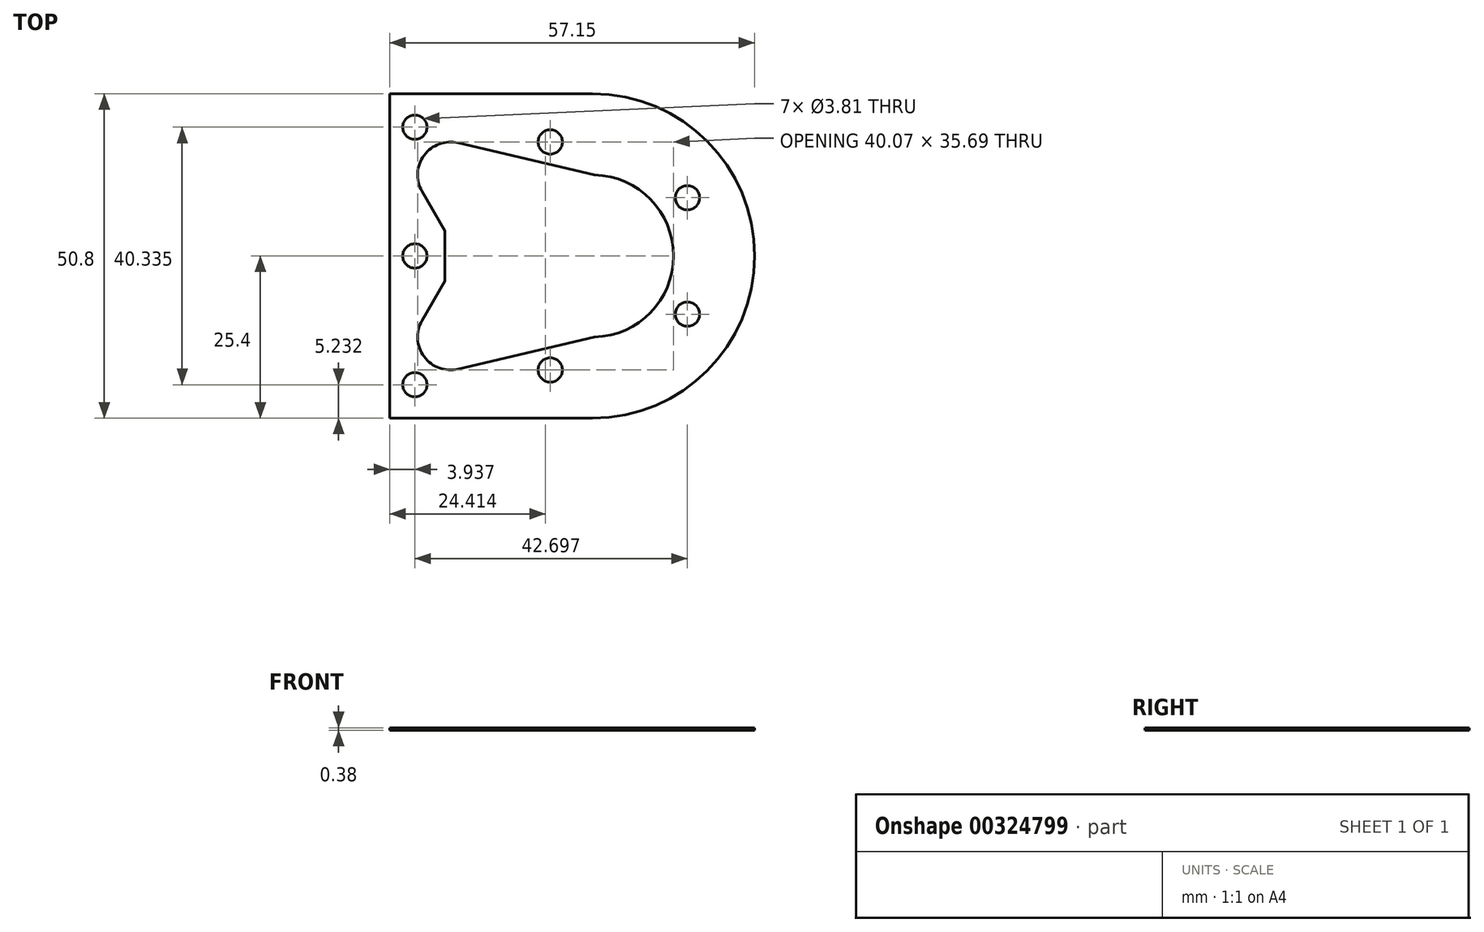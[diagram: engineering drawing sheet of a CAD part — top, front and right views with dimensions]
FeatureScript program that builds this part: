
annotation { "Feature Type Name" : "Feature", "Feature Type Description" : "" }
export const myFeature = defineFeature(function(context is Context, id is Id, definition is map)
    precondition{}
    {
        {
            var Q0;
            Q0=qCreatedBy(makeId("Top.planeOp"),FACE);
            var sketch = newSketch(context, id + "F0", { "sketchPlane" : qUnion([Q0])});
            skLineSegment(sketch, "E0", {"start": v(0, 25.4) * mm, "end": v(31.75, 25.4) * mm});
            skLineSegment(sketch, "E1.MirrorCS", {"start": v(0, -25.4) * mm, "end": v(31.75, -25.4) * mm});
            skArc(sketch, "E2", {"start": v(31.75, 25.4) * mm, "mid": v(57.15, 0) * mm, "end": v(31.75, -25.4) * mm});
            skLineSegment(sketch, "E3", {"start": v(0, 25.4) * mm, "end": v(0, -25.4) * mm});
            skArc(sketch, "E4", {"start": v(32.09, -12.7) * mm, "mid": v(44.45, 0) * mm, "end": v(32.09, 12.7) * mm});
            skArc(sketch, "E5", {"start": v(10.7, 17.72) * mm, "mid": v(5.39, 15.78) * mm, "end": v(5.06, 10.12) * mm});
            skArc(sketch, "E6.MirrorC", {"start": v(10.7, -17.72) * mm, "mid": v(5.39, -15.78) * mm, "end": v(5.06, -10.12) * mm});
            skLineSegment(sketch, "E7", {"start": v(32.09, 12.7) * mm, "end": v(10.7, 17.72) * mm});
            skLineSegment(sketch, "E8.MirrorCS", {"start": v(32.09, -12.7) * mm, "end": v(10.7, -17.72) * mm});
            skLineSegment(sketch, "E9", {"start": v(8.64, 3.93) * mm, "end": v(8.64, -3.93) * mm});
            skLineSegment(sketch, "E10", {"start": v(5.06, 10.12) * mm, "end": v(8.64, 3.93) * mm});
            skPoint(sketch, "E11.orphan", {"position": v(8.64, 7.62) * mm});
            skLineSegment(sketch, "E12.MirrorCS", {"start": v(5.06, -10.12) * mm, "end": v(8.64, -3.93) * mm});
            skSolve(sketch);
        }
        {
            var Q0;
            Q0=makeQuery(id+"F0.imprint","IMPRINT",FACE,{"disambiguationData":[TD([[makeQuery(id+"F0.imprint","IMPRINT",EDGE,{"derivedFrom":sQuery(id+"F0.wireOp",EDGE,"E0")}),-1.0]])]});
            extrude(context, id + "F1", {"entities" : qUnion([Q0]), "depth" : 0.38 * mm, "offsetDistance" : 25.4 * mm});
        }
        {
            var Q0;
            Q0=makeQuery(id+"F1.opExtrude","CAP_FACE",FACE,{"disambiguationData":[OSD([sQuery(id+"F0.wireOp",EDGE,"E0"),sQuery(id+"F0.wireOp",EDGE,"E1.MirrorCS"),sQuery(id+"F0.wireOp",EDGE,"E2"),sQuery(id+"F0.wireOp",EDGE,"E3"),sQuery(id+"F0.wireOp",EDGE,"E4"),sQuery(id+"F0.wireOp",EDGE,"E5"),sQuery(id+"F0.wireOp",EDGE,"E6.MirrorC"),sQuery(id+"F0.wireOp",EDGE,"E7"),sQuery(id+"F0.wireOp",EDGE,"E8.MirrorCS"),sQuery(id+"F0.wireOp",EDGE,"E9"),sQuery(id+"F0.wireOp",EDGE,"E10"),sQuery(id+"F0.wireOp",EDGE,"E12.MirrorCS")])],"isStart":false});
            var sketch = newSketch(context, id + "F2", { "sketchPlane" : qUnion([Q0])});
            skPoint(sketch, "E13", {"position": v(3.94, 0) * mm});
            skPoint(sketch, "E14", {"position": v(3.94, 20.17) * mm});
            skPoint(sketch, "E15", {"position": v(3.94, -20.17) * mm});
            skPoint(sketch, "E16", {"position": v(25.15, 17.86) * mm});
            skPoint(sketch, "E17", {"position": v(25.15, -17.86) * mm});
            skPoint(sketch, "E18", {"position": v(46.63, 9.12) * mm});
            skPoint(sketch, "E19", {"position": v(46.63, -9.12) * mm});
            skSolve(sketch);
        }
        {
            var Q0;
            Q0=sQuery(id+"F2.wireOp",VERTEX,"E14");
            var Q1;
            Q1=sQuery(id+"F2.wireOp",VERTEX,"E13");
            var Q2;
            Q2=sQuery(id+"F2.wireOp",VERTEX,"E15");
            var Q3;
            Q3=sQuery(id+"F2.wireOp",VERTEX,"E17");
            var Q4;
            Q4=sQuery(id+"F2.wireOp",VERTEX,"E19");
            var Q5;
            Q5=sQuery(id+"F2.wireOp",VERTEX,"E18");
            var Q6;
            Q6=sQuery(id+"F2.wireOp",VERTEX,"E16");
            var Q7;
            Q7=makeQuery(id+"F1.opExtrude","SWEPT_BODY",BODY,{"disambiguationData":[OSD([sQuery(id+"F0.wireOp",EDGE,"E0"),sQuery(id+"F0.wireOp",EDGE,"E1.MirrorCS"),sQuery(id+"F0.wireOp",EDGE,"E2"),sQuery(id+"F0.wireOp",EDGE,"E3"),sQuery(id+"F0.wireOp",EDGE,"E4"),sQuery(id+"F0.wireOp",EDGE,"E5"),sQuery(id+"F0.wireOp",EDGE,"E6.MirrorC"),sQuery(id+"F0.wireOp",EDGE,"E7"),sQuery(id+"F0.wireOp",EDGE,"E8.MirrorCS"),sQuery(id+"F0.wireOp",EDGE,"E9"),sQuery(id+"F0.wireOp",EDGE,"E10"),sQuery(id+"F0.wireOp",EDGE,"E12.MirrorCS")])]});
            hole(context, id + "F3", {"style" : HoleStyle.SIMPLE, "endStyle" : HoleEndStyle.THROUGH, "holeDiameter" : 3.8 * mm, "majorDiameter" : 6.35 * mm, "tappedDepth" : 12.7 * mm, "tapClearance" : 3, "locations" : qUnion([Q0, Q1, Q2, Q3, Q4, Q5, Q6]), "scope" : qUnion([Q7])});
        }
    });
